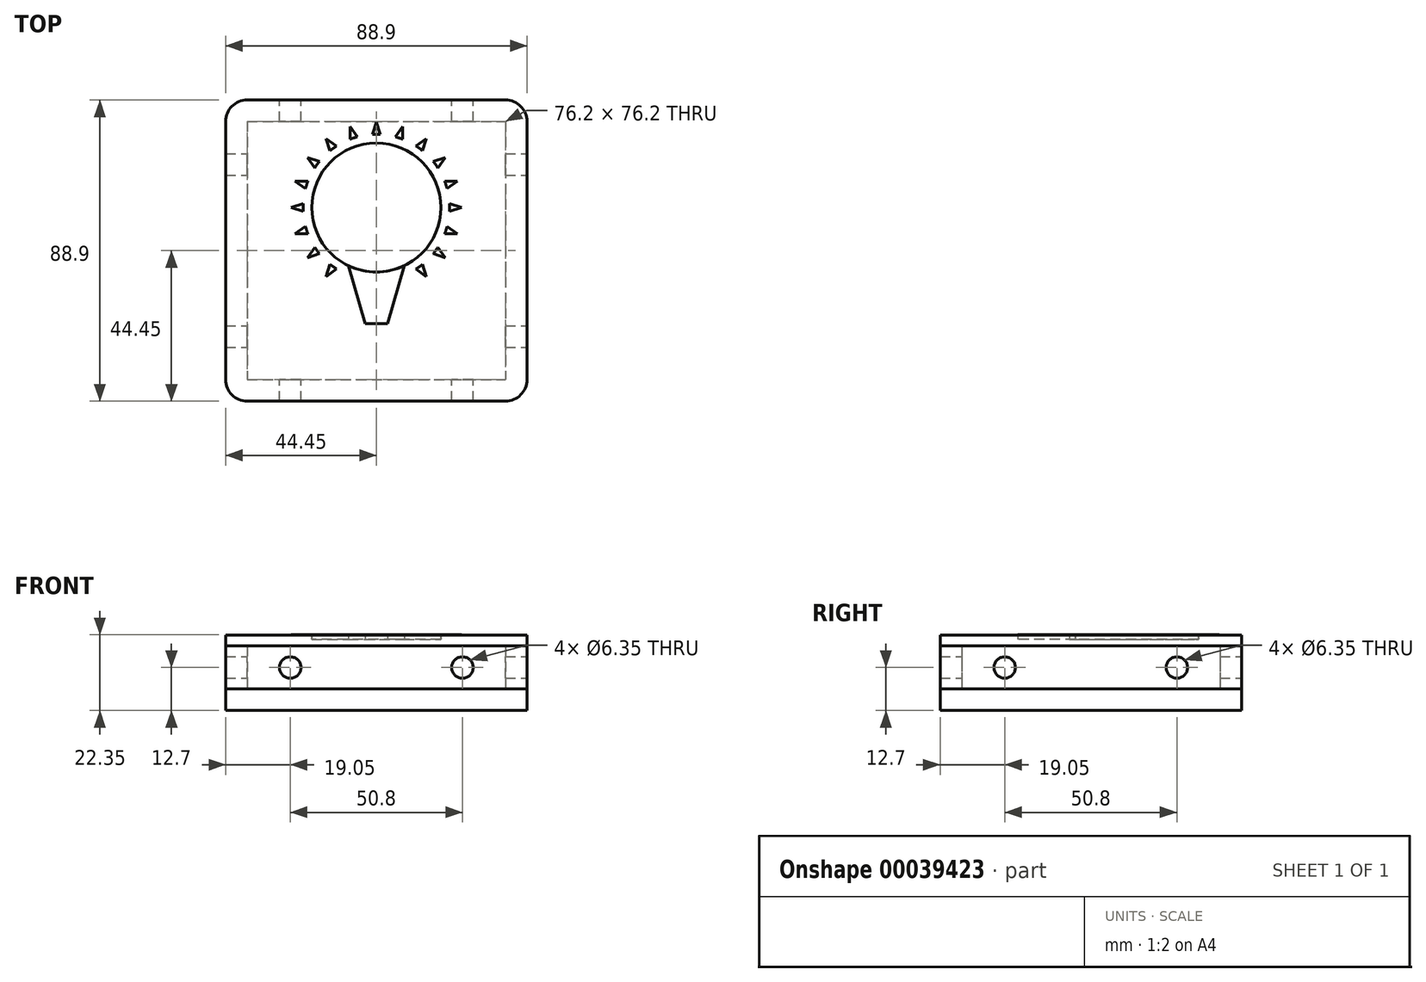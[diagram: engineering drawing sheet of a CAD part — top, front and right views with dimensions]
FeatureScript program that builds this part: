
annotation { "Feature Type Name" : "Feature", "Feature Type Description" : "" }
export const myFeature = defineFeature(function(context is Context, id is Id, definition is map)
    precondition{}
    {
        {
            var Q0;
            Q0=qCreatedBy(makeId("Top.planeOp"),FACE);
            var sketch = newSketch(context, id + "F0", { "sketchPlane" : qUnion([Q0])});
            skLineSegment(sketch, "E0.rect.bottom", {"start": v(-38.1, 44.45) * mm, "end": v(38.1, 44.45) * mm});
            skLineSegment(sketch, "E0.rect.top", {"start": v(-38.1, -44.45) * mm, "end": v(38.1, -44.45) * mm});
            skLineSegment(sketch, "E0.rect.left", {"start": v(-44.45, 38.1) * mm, "end": v(-44.45, -38.1) * mm});
            skLineSegment(sketch, "E0.rect.right", {"start": v(44.45, 38.1) * mm, "end": v(44.45, -38.1) * mm});
            skPoint(sketch, "E0.rect.middle", {"position": v(0, 0) * mm});
            skPoint(sketch, "E1.visualSharp", {"position": v(-44.45, 44.45) * mm});
            skArc(sketch, "E1.filletArc", {"start": v(-38.1, 44.45) * mm, "mid": v(-42.6, 42.6) * mm, "end": v(-44.45, 38.1) * mm});
            skPoint(sketch, "E2.visualSharp", {"position": v(44.45, 44.45) * mm});
            skArc(sketch, "E2.filletArc", {"start": v(44.45, 38.1) * mm, "mid": v(42.6, 42.6) * mm, "end": v(38.1, 44.45) * mm});
            skPoint(sketch, "E3.visualSharp", {"position": v(44.45, -44.45) * mm});
            skArc(sketch, "E3.filletArc", {"start": v(38.1, -44.45) * mm, "mid": v(42.6, -42.6) * mm, "end": v(44.45, -38.1) * mm});
            skPoint(sketch, "E4.visualSharp", {"position": v(-44.45, -44.45) * mm});
            skArc(sketch, "E4.filletArc", {"start": v(-44.45, -38.1) * mm, "mid": v(-42.6, -42.6) * mm, "end": v(-38.1, -44.45) * mm});
            skSolve(sketch);
        }
        {
            var Q0;
            Q0 = qSketchRegion(id + "F0", true);
            extrude(context, id + "F1", {"entities" : qUnion([Q0]), "depth" : 6.35 * mm});
        }
        {
            var Q0;
            Q0=makeQuery(id+"F1.opExtrude","CAP_FACE",FACE,{"disambiguationData":[OSD([sQuery(id+"F0.wireOp",EDGE,"E0.rect.bottom"),sQuery(id+"F0.wireOp",EDGE,"E0.rect.top"),sQuery(id+"F0.wireOp",EDGE,"E0.rect.left"),sQuery(id+"F0.wireOp",EDGE,"E0.rect.right"),sQuery(id+"F0.wireOp",EDGE,"E1.filletArc"),sQuery(id+"F0.wireOp",EDGE,"E2.filletArc"),sQuery(id+"F0.wireOp",EDGE,"E3.filletArc"),sQuery(id+"F0.wireOp",EDGE,"E4.filletArc")])],"isStart":false});
            var sketch = newSketch(context, id + "F2", { "sketchPlane" : qUnion([Q0])});
            skArc(sketch, "E5.0", {"start": v(-38.1, 44.45) * mm, "mid": v(-42.6, 42.6) * mm, "end": v(-44.45, 38.1) * mm});
            skLineSegment(sketch, "E6.0", {"start": v(-38.1, 44.45) * mm, "end": v(38.1, 44.45) * mm});
            skArc(sketch, "E7.0", {"start": v(44.45, 38.1) * mm, "mid": v(42.6, 42.6) * mm, "end": v(38.1, 44.45) * mm});
            skLineSegment(sketch, "E8.0", {"start": v(44.45, 38.1) * mm, "end": v(44.45, -38.1) * mm});
            skArc(sketch, "E9.0", {"start": v(38.1, -44.45) * mm, "mid": v(42.6, -42.6) * mm, "end": v(44.45, -38.1) * mm});
            skLineSegment(sketch, "E10.0", {"start": v(-38.1, -44.45) * mm, "end": v(38.1, -44.45) * mm});
            skArc(sketch, "E11.0", {"start": v(-44.45, -38.1) * mm, "mid": v(-42.6, -42.6) * mm, "end": v(-38.1, -44.45) * mm});
            skLineSegment(sketch, "E12.0", {"start": v(-44.45, 38.1) * mm, "end": v(-44.45, -38.1) * mm});
            skLineSegment(sketch, "E13", {"start": v(-44.45, -38.1) * mm, "end": v(44.45, -38.1) * mm});
            skLineSegment(sketch, "E14", {"start": v(-44.45, 38.1) * mm, "end": v(44.45, 38.1) * mm});
            skLineSegment(sketch, "E15", {"start": v(38.1, 38.1) * mm, "end": v(38.1, -38.1) * mm});
            skLineSegment(sketch, "E16", {"start": v(-38.1, 38.1) * mm, "end": v(-38.1, -38.1) * mm});
            skSolve(sketch);
        }
        {
            var Q0;
            Q0 = qSketchRegion(id + "F2", true);
            extrude(context, id + "F3", {"entities" : qUnion([Q0]), "depth" : 12.7 * mm});
        }
        {
            var Q0;
            Q0=makeQuery(id+"F3.opExtrude","CAP_FACE",FACE,{"disambiguationData":[OSD([sQuery(id+"F2.wireOp",EDGE,"E5.0"),sQuery(id+"F2.wireOp",EDGE,"E6.0"),sQuery(id+"F2.wireOp",EDGE,"E7.0"),sQuery(id+"F2.wireOp",EDGE,"E8.0"),sQuery(id+"F2.wireOp",EDGE,"E9.0"),sQuery(id+"F2.wireOp",EDGE,"E10.0"),sQuery(id+"F2.wireOp",EDGE,"E11.0"),sQuery(id+"F2.wireOp",EDGE,"E12.0"),sQuery(id+"F2.wireOp",EDGE,"E13"),sQuery(id+"F2.wireOp",EDGE,"E14"),sQuery(id+"F2.wireOp",EDGE,"E15"),sQuery(id+"F2.wireOp",EDGE,"E16")])],"isStart":false});
            var sketch = newSketch(context, id + "F4", { "sketchPlane" : qUnion([Q0])});
            skArc(sketch, "E17.0", {"start": v(-38.1, 44.45) * mm, "mid": v(-42.6, 42.6) * mm, "end": v(-44.45, 38.1) * mm});
            skLineSegment(sketch, "E18.0", {"start": v(-38.1, 44.45) * mm, "end": v(38.1, 44.45) * mm});
            skArc(sketch, "E19.0", {"start": v(44.45, 38.1) * mm, "mid": v(42.6, 42.6) * mm, "end": v(38.1, 44.45) * mm});
            skLineSegment(sketch, "E20.0", {"start": v(44.45, 38.1) * mm, "end": v(44.45, -38.1) * mm});
            skArc(sketch, "E21.0", {"start": v(38.1, -44.45) * mm, "mid": v(42.6, -42.6) * mm, "end": v(44.45, -38.1) * mm});
            skLineSegment(sketch, "E22.0", {"start": v(-38.1, -44.45) * mm, "end": v(38.1, -44.45) * mm});
            skArc(sketch, "E23.0", {"start": v(-44.45, -38.1) * mm, "mid": v(-42.6, -42.6) * mm, "end": v(-38.1, -44.45) * mm});
            skLineSegment(sketch, "E24.0", {"start": v(-44.45, 38.1) * mm, "end": v(-44.45, -38.1) * mm});
            skSolve(sketch);
        }
        {
            var Q0;
            Q0 = qSketchRegion(id + "F4", true);
            extrude(context, id + "F5", {"entities" : qUnion([Q0]), "depth" : 3.17 * mm});
        }
        {
            var Q0;
            Q0=makeQuery(id+"F3.opExtrude","SWEPT_FACE",FACE,{"disambiguationData":[OSD([sQuery(id+"F2.wireOp",EDGE,"E8.0")])]});
            var sketch = newSketch(context, id + "F6", { "sketchPlane" : qUnion([Q0])});
            skCircle(sketch, "E25", {"center": v(25.4, 12.7) * mm, "radius": 3.18 * mm});
            skPoint(sketch, "E25.centerSnap0", {"position": v(38.1, 12.7) * mm});
            skCircle(sketch, "E26", {"center": v(-25.4, 12.7) * mm, "radius": 3.18 * mm});
            skPoint(sketch, "E26.centerSnap0", {"position": v(-38.1, 12.7) * mm});
            skSolve(sketch);
        }
        {
            var Q0;
            Q0 = qSketchRegion(id + "F6", true);
            extrude(context, id + "F7", {"entities" : qUnion([Q0]), "operationType" : NewBodyOperationType.REMOVE, "endBound" : BoundingType.THROUGH_ALL, "oppositeDirection" : true, "depth" : 25.4 * mm});
        }
        {
            var Q0;
            Q0=makeQuery(id+"F3.opExtrude","SWEPT_FACE",FACE,{"disambiguationData":[OSD([sQuery(id+"F2.wireOp",EDGE,"E6.0")])]});
            var sketch = newSketch(context, id + "F8", { "sketchPlane" : qUnion([Q0])});
            skCircle(sketch, "E27", {"center": v(25.4, 12.7) * mm, "radius": 3.18 * mm});
            skPoint(sketch, "E27.centerSnap0", {"position": v(38.1, 12.7) * mm});
            skCircle(sketch, "E28", {"center": v(-25.4, 12.7) * mm, "radius": 3.18 * mm});
            skSolve(sketch);
        }
        {
            var Q0;
            Q0 = qSketchRegion(id + "F8", true);
            extrude(context, id + "F9", {"entities" : qUnion([Q0]), "operationType" : NewBodyOperationType.REMOVE, "endBound" : BoundingType.THROUGH_ALL, "oppositeDirection" : true, "depth" : 25.4 * mm});
        }
        {
            var Q0;
            Q0=makeQuery(id+"F5.opExtrude","CAP_FACE",FACE,{"disambiguationData":[OSD([sQuery(id+"F4.wireOp",EDGE,"E17.0"),sQuery(id+"F4.wireOp",EDGE,"E18.0"),sQuery(id+"F4.wireOp",EDGE,"E19.0"),sQuery(id+"F4.wireOp",EDGE,"E20.0"),sQuery(id+"F4.wireOp",EDGE,"E21.0"),sQuery(id+"F4.wireOp",EDGE,"E22.0"),sQuery(id+"F4.wireOp",EDGE,"E23.0"),sQuery(id+"F4.wireOp",EDGE,"E24.0")])],"isStart":false});
            var sketch = newSketch(context, id + "F10", { "sketchPlane" : qUnion([Q0])});
            skLineSegment(sketch, "E29.rect.bottom", {"start": v(-10.16, 22.86) * mm, "end": v(-3.8, 22.86) * mm});
            skLineSegment(sketch, "E29.rect.top", {"start": v(-10.16, -22.86) * mm, "end": v(10.16, -22.86) * mm});
            skLineSegment(sketch, "E29.rect.left", {"start": v(-12.7, 20.32) * mm, "end": v(-12.7, -20.32) * mm});
            skLineSegment(sketch, "E29.rect.right", {"start": v(12.7, 20.32) * mm, "end": v(12.7, -20.32) * mm});
            skPoint(sketch, "E29.rect.middle", {"position": v(0, 0) * mm});
            skLineSegment(sketch, "E30.rect.top", {"start": v(3.81, 29.21) * mm, "end": v(-3.8, 29.21) * mm});
            skLineSegment(sketch, "E30.rect.left", {"start": v(3.81, 22.86) * mm, "end": v(3.81, 29.21) * mm});
            skLineSegment(sketch, "E30.rect.right", {"start": v(-3.8, 22.86) * mm, "end": v(-3.8, 29.21) * mm});
            skPoint(sketch, "E30.rect.middle", {"position": v(0, 26.04) * mm});
            skLineSegment(sketch, "E31.trimOffspring", {"start": v(3.81, 22.86) * mm, "end": v(10.16, 22.86) * mm});
            skPoint(sketch, "E32.visualSharp", {"position": v(-12.7, 22.86) * mm});
            skArc(sketch, "E32.filletArc", {"start": v(-10.16, 22.86) * mm, "mid": v(-11.96, 22.12) * mm, "end": v(-12.7, 20.32) * mm});
            skPoint(sketch, "E33.visualSharp", {"position": v(12.7, 22.86) * mm});
            skArc(sketch, "E33.filletArc", {"start": v(12.7, 20.32) * mm, "mid": v(11.96, 22.12) * mm, "end": v(10.16, 22.86) * mm});
            skPoint(sketch, "E34.visualSharp", {"position": v(12.7, -22.86) * mm});
            skArc(sketch, "E34.filletArc", {"start": v(10.16, -22.86) * mm, "mid": v(11.96, -22.12) * mm, "end": v(12.7, -20.32) * mm});
            skPoint(sketch, "E35.visualSharp", {"position": v(-12.7, -22.86) * mm});
            skArc(sketch, "E35.filletArc", {"start": v(-12.7, -20.32) * mm, "mid": v(-11.96, -22.12) * mm, "end": v(-10.16, -22.86) * mm});
            skLineSegment(sketch, "E36", {"start": v(-2.4, 27.75) * mm, "end": v(2.54, 27.75) * mm});
            skLineSegment(sketch, "E37", {"start": v(2.54, 27.75) * mm, "end": v(2.54, 21.52) * mm});
            skLineSegment(sketch, "E38", {"start": v(2.54, 21.52) * mm, "end": v(10.71, 21.52) * mm});
            skLineSegment(sketch, "E39", {"start": v(10.71, 21.52) * mm, "end": v(10.71, -20.32) * mm});
            skLineSegment(sketch, "E40", {"start": v(10.71, -20.32) * mm, "end": v(-11.48, -20.32) * mm});
            skLineSegment(sketch, "E41", {"start": v(-11.48, -20.32) * mm, "end": v(-11.48, 21.52) * mm});
            skLineSegment(sketch, "E42", {"start": v(-11.48, 21.52) * mm, "end": v(-2.4, 21.52) * mm});
            skLineSegment(sketch, "E43", {"start": v(-2.4, 21.52) * mm, "end": v(-2.4, 27.75) * mm});
            skLineSegment(sketch, "E44.rect.bottom", {"start": v(-9.14, 19.32) * mm, "end": v(9.14, 19.32) * mm});
            skLineSegment(sketch, "E44.rect.top", {"start": v(-9.14, 6.86) * mm, "end": v(9.14, 6.86) * mm});
            skLineSegment(sketch, "E44.rect.left", {"start": v(-9.14, 19.32) * mm, "end": v(-9.14, 6.86) * mm});
            skLineSegment(sketch, "E44.rect.right", {"start": v(9.14, 19.32) * mm, "end": v(9.14, 6.86) * mm});
            skPoint(sketch, "E44.rect.middle", {"position": v(0, 13.09) * mm});
            skLineSegment(sketch, "E45.bottom", {"start": v(-9.14, 4.65) * mm, "end": v(9.14, 4.65) * mm});
            skLineSegment(sketch, "E45.top", {"start": v(-9.14, -6.5) * mm, "end": v(9.14, -6.5) * mm});
            skLineSegment(sketch, "E45.left", {"start": v(-9.14, 4.65) * mm, "end": v(-9.14, -6.5) * mm});
            skLineSegment(sketch, "E45.right", {"start": v(9.14, 4.65) * mm, "end": v(9.14, -6.5) * mm});
            skLineSegment(sketch, "E46.bottom", {"start": v(-9.14, -8.32) * mm, "end": v(9.14, -8.32) * mm});
            skLineSegment(sketch, "E46.top", {"start": v(-9.14, -18.83) * mm, "end": v(9.14, -18.83) * mm});
            skLineSegment(sketch, "E46.left", {"start": v(-9.14, -8.32) * mm, "end": v(-9.14, -18.83) * mm});
            skLineSegment(sketch, "E46.right", {"start": v(9.14, -8.32) * mm, "end": v(9.14, -18.83) * mm});
            skSolve(sketch);
        }
        {
            var Q0;
            Q0 = qSketchRegion(id + "F10", true);
            var Q1;
            Q1=makeQuery(id+"F10.imprint","IMPRINT",FACE,{"disambiguationData":[TD([[makeQuery(id+"F10.imprint","IMPRINT",EDGE,{"derivedFrom":sQuery(id+"F10.wireOp",EDGE,"E44.rect.bottom")}),-1.0]])]});
            var Q2;
            Q2=makeQuery(id+"F10.imprint","IMPRINT",FACE,{"disambiguationData":[TD([[makeQuery(id+"F10.imprint","IMPRINT",EDGE,{"derivedFrom":sQuery(id+"F10.wireOp",EDGE,"E45.bottom")}),-1.0]])]});
            var Q3;
            Q3=makeQuery(id+"F10.imprint","IMPRINT",FACE,{"disambiguationData":[TD([[makeQuery(id+"F10.imprint","IMPRINT",EDGE,{"derivedFrom":sQuery(id+"F10.wireOp",EDGE,"E46.bottom")}),-1.0]])]});
            extrude(context, id + "F11", {"entities" : qUnion([Q0, Q1, Q2, Q3]), "operationType" : NewBodyOperationType.REMOVE, "oppositeDirection" : true, "depth" : 1.27 * mm});
        }
        {
            var Q0;
            Q0=makeQuery(id+"F3.opExtrude","CAP_FACE",FACE,{"disambiguationData":[OSD([sQuery(id+"F2.wireOp",EDGE,"E5.0"),sQuery(id+"F2.wireOp",EDGE,"E6.0"),sQuery(id+"F2.wireOp",EDGE,"E7.0"),sQuery(id+"F2.wireOp",EDGE,"E8.0"),sQuery(id+"F2.wireOp",EDGE,"E9.0"),sQuery(id+"F2.wireOp",EDGE,"E10.0"),sQuery(id+"F2.wireOp",EDGE,"E11.0"),sQuery(id+"F2.wireOp",EDGE,"E12.0"),sQuery(id+"F2.wireOp",EDGE,"E13"),sQuery(id+"F2.wireOp",EDGE,"E14"),sQuery(id+"F2.wireOp",EDGE,"E15"),sQuery(id+"F2.wireOp",EDGE,"E16")])],"isStart":false});
            var sketch = newSketch(context, id + "F12", { "sketchPlane" : qUnion([Q0])});
            skArc(sketch, "E47.0", {"start": v(-38.1, 44.45) * mm, "mid": v(-42.6, 42.6) * mm, "end": v(-44.45, 38.1) * mm});
            skLineSegment(sketch, "E48.0", {"start": v(-38.1, 44.45) * mm, "end": v(38.1, 44.45) * mm});
            skArc(sketch, "E49.0", {"start": v(44.45, 38.1) * mm, "mid": v(42.6, 42.6) * mm, "end": v(38.1, 44.45) * mm});
            skLineSegment(sketch, "E50.0", {"start": v(44.45, 38.1) * mm, "end": v(44.45, -38.1) * mm});
            skArc(sketch, "E51.0", {"start": v(38.1, -44.45) * mm, "mid": v(42.6, -42.6) * mm, "end": v(44.45, -38.1) * mm});
            skLineSegment(sketch, "E52.0", {"start": v(-38.1, -44.45) * mm, "end": v(38.1, -44.45) * mm});
            skArc(sketch, "E53.0", {"start": v(-44.45, -38.1) * mm, "mid": v(-42.6, -42.6) * mm, "end": v(-38.1, -44.45) * mm});
            skLineSegment(sketch, "E54.0", {"start": v(-44.45, 38.1) * mm, "end": v(-44.45, -38.1) * mm});
            skSolve(sketch);
        }
        {
            var Q0;
            Q0 = qSketchRegion(id + "F12", true);
            extrude(context, id + "F13", {"entities" : qUnion([Q0]), "depth" : 3.17 * mm});
        }
        {
            var Q0;
            Q0=makeQuery(id+"F13.opExtrude","CAP_FACE",FACE,{"disambiguationData":[OSD([sQuery(id+"F12.wireOp",EDGE,"E47.0"),sQuery(id+"F12.wireOp",EDGE,"E48.0"),sQuery(id+"F12.wireOp",EDGE,"E49.0"),sQuery(id+"F12.wireOp",EDGE,"E50.0"),sQuery(id+"F12.wireOp",EDGE,"E51.0"),sQuery(id+"F12.wireOp",EDGE,"E52.0"),sQuery(id+"F12.wireOp",EDGE,"E53.0"),sQuery(id+"F12.wireOp",EDGE,"E54.0")])],"isStart":false});
            var sketch = newSketch(context, id + "F14", { "sketchPlane" : qUnion([Q0])});
            skCircle(sketch, "E55", {"center": v(0, 12.7) * mm, "radius": 19.05 * mm});
            skPoint(sketch, "E55.centerSnap0", {"position": v(0, -44.45) * mm});
            skLineSegment(sketch, "E56", {"start": v(-8.25, -4.47) * mm, "end": v(-3.35, -21.59) * mm});
            skLineSegment(sketch, "E57", {"start": v(-3.35, -21.59) * mm, "end": v(0, -21.59) * mm});
            skLineSegment(sketch, "E58", {"start": v(0, -21.59) * mm, "end": v(0, -6.35) * mm});
            skLineSegment(sketch, "E59.MirrorCS", {"start": v(3.35, -21.59) * mm, "end": v(0, -21.59) * mm});
            skLineSegment(sketch, "E60.MirrorCS", {"start": v(8.26, -4.47) * mm, "end": v(3.35, -21.6) * mm});
            skSolve(sketch);
        }
        {
            var Q0;
            Q0 = qSketchRegion(id + "F14", true);
            extrude(context, id + "F15", {"entities" : qUnion([Q0]), "operationType" : NewBodyOperationType.REMOVE, "oppositeDirection" : true, "depth" : 1.27 * mm});
        }
        {
            var Q0;
            Q0=makeQuery(id+"F15.boolean.opBoolean","COPY",FACE,{"derivedFrom":makeQuery(id+"F15.opExtrude","CAP_FACE",FACE,{"disambiguationData":[OSD([sQuery(id+"F14.wireOp",EDGE,"E55"),sQuery(id+"F14.wireOp",EDGE,"E56"),sQuery(id+"F14.wireOp",EDGE,"E57"),sQuery(id+"F14.wireOp",EDGE,"E59.MirrorCS"),sQuery(id+"F14.wireOp",EDGE,"E60.MirrorCS")])],"isStart":false})});
            var sketch = newSketch(context, id + "F16", { "sketchPlane" : qUnion([Q0])});
            skArc(sketch, "E61.0", {"start": v(8.26, -4.47) * mm, "mid": v(0, 31.75) * mm, "end": v(-8.25, -4.47) * mm});
            skCircle(sketch, "E62", {"center": v(0, 12.7) * mm, "radius": 19.05 * mm});
            skSolve(sketch);
        }
        {
            var Q0;
            Q0 = qSketchRegion(id + "F16", true);
            extrude(context, id + "F17", {"entities" : qUnion([Q0]), "depth" : 1.4 * mm});
        }
        {
            var Q0;
            Q0=makeQuery(id+"F15.boolean.opBoolean","COPY",FACE,{"derivedFrom":makeQuery(id+"F15.opExtrude","CAP_FACE",FACE,{"disambiguationData":[OSD([sQuery(id+"F14.wireOp",EDGE,"E55"),sQuery(id+"F14.wireOp",EDGE,"E56"),sQuery(id+"F14.wireOp",EDGE,"E57"),sQuery(id+"F14.wireOp",EDGE,"E59.MirrorCS"),sQuery(id+"F14.wireOp",EDGE,"E60.MirrorCS")])],"isStart":false})});
            var sketch = newSketch(context, id + "F18", { "sketchPlane" : qUnion([Q0])});
            skArc(sketch, "E63.0.0", {"start": v(8.26, -4.47) * mm, "mid": v(0, 31.75) * mm, "end": v(-8.25, -4.47) * mm});
            skLineSegment(sketch, "E63.0.1", {"start": v(-8.25, -4.47) * mm, "end": v(-3.35, -21.59) * mm});
            skLineSegment(sketch, "E63.0.2", {"start": v(-3.35, -21.59) * mm, "end": v(3.35, -21.59) * mm});
            skLineSegment(sketch, "E63.0.3", {"start": v(3.35, -21.6) * mm, "end": v(8.26, -4.47) * mm});
            skCircle(sketch, "E64.0", {"center": v(0, 12.7) * mm, "radius": 19.05 * mm});
            skSolve(sketch);
        }
        {
            var Q0;
            {var subQ2=sQuery(id+"F18.wireOp",EDGE,"E63.0.1");Q0=makeQuery(id+"F18.imprint","IMPRINT",FACE,{"disambiguationData":[TD([[makeQuery(id+"F18.imprint","IMPRINT",EDGE,{"derivedFrom":subQ2}),1.0]])]});}
            extrude(context, id + "F19", {"entities" : qUnion([Q0]), "depth" : 1.4 * mm});
        }
        {
            var Q0;
            Q0=makeQuery(id+"F13.opExtrude","CAP_FACE",FACE,{"disambiguationData":[OSD([sQuery(id+"F12.wireOp",EDGE,"E47.0"),sQuery(id+"F12.wireOp",EDGE,"E48.0"),sQuery(id+"F12.wireOp",EDGE,"E49.0"),sQuery(id+"F12.wireOp",EDGE,"E50.0"),sQuery(id+"F12.wireOp",EDGE,"E51.0"),sQuery(id+"F12.wireOp",EDGE,"E52.0"),sQuery(id+"F12.wireOp",EDGE,"E53.0"),sQuery(id+"F12.wireOp",EDGE,"E54.0")])],"isStart":false});
            var sketch = newSketch(context, id + "F20", { "sketchPlane" : qUnion([Q0])});
            skCircle(sketch, "E65", {"center": v(0, 12.7) * mm, "radius": 21.61 * mm});
            skLineSegment(sketch, "E66", {"start": v(0, 34.31) * mm, "end": v(0, 37.87) * mm});
            skPoint(sketch, "E66.startSnap0", {"position": v(0, 31.75) * mm});
            skLineSegment(sketch, "E67", {"start": v(0, 37.87) * mm, "end": v(-1.17, 34.28) * mm});
            skLineSegment(sketch, "E68.MirrorCS", {"start": v(0, 37.87) * mm, "end": v(1.17, 34.28) * mm});
            skLineSegment(sketch, "E69.1.0", {"start": v(-7.78, 36.64) * mm, "end": v(-5.56, 33.59) * mm});
            skLineSegment(sketch, "E69.1.1", {"start": v(-7.78, 36.64) * mm, "end": v(-7.78, 32.86) * mm});
            skLineSegment(sketch, "E69.2.0", {"start": v(-14.8, 33.07) * mm, "end": v(-11.74, 30.85) * mm});
            skLineSegment(sketch, "E69.2.1", {"start": v(-14.8, 33.07) * mm, "end": v(-13.63, 29.47) * mm});
            skLineSegment(sketch, "E69.3.0", {"start": v(-20.37, 27.5) * mm, "end": v(-16.77, 26.33) * mm});
            skLineSegment(sketch, "E69.3.1", {"start": v(-20.37, 27.5) * mm, "end": v(-18.15, 24.44) * mm});
            skLineSegment(sketch, "E69.4.0", {"start": v(-23.94, 20.48) * mm, "end": v(-20.16, 20.48) * mm});
            skLineSegment(sketch, "E69.4.1", {"start": v(-23.94, 20.48) * mm, "end": v(-20.89, 18.26) * mm});
            skLineSegment(sketch, "E69.5.0", {"start": v(-25.17, 12.7) * mm, "end": v(-21.58, 13.87) * mm});
            skLineSegment(sketch, "E69.5.1", {"start": v(-25.17, 12.7) * mm, "end": v(-21.58, 11.53) * mm});
            skLineSegment(sketch, "E69.6.0", {"start": v(-23.94, 4.92) * mm, "end": v(-20.89, 7.14) * mm});
            skLineSegment(sketch, "E69.6.1", {"start": v(-23.94, 4.92) * mm, "end": v(-20.16, 4.92) * mm});
            skLineSegment(sketch, "E69.7.0", {"start": v(-20.37, -2.1) * mm, "end": v(-18.15, 0.96) * mm});
            skLineSegment(sketch, "E69.7.1", {"start": v(-20.37, -2.1) * mm, "end": v(-16.77, -0.93) * mm});
            skLineSegment(sketch, "E69.8.0", {"start": v(-14.8, -7.67) * mm, "end": v(-13.63, -4.07) * mm});
            skLineSegment(sketch, "E69.8.1", {"start": v(-14.8, -7.67) * mm, "end": v(-11.74, -5.45) * mm});
            skLineSegment(sketch, "E69.12.0", {"start": v(14.8, -7.67) * mm, "end": v(11.74, -5.45) * mm});
            skLineSegment(sketch, "E69.12.1", {"start": v(14.8, -7.67) * mm, "end": v(13.63, -4.07) * mm});
            skLineSegment(sketch, "E69.13.0", {"start": v(20.37, -2.1) * mm, "end": v(16.77, -0.93) * mm});
            skLineSegment(sketch, "E69.13.1", {"start": v(20.37, -2.1) * mm, "end": v(18.15, 0.96) * mm});
            skLineSegment(sketch, "E69.14.0", {"start": v(23.94, 4.92) * mm, "end": v(20.16, 4.92) * mm});
            skLineSegment(sketch, "E69.14.1", {"start": v(23.94, 4.92) * mm, "end": v(20.89, 7.14) * mm});
            skLineSegment(sketch, "E69.15.0", {"start": v(25.17, 12.7) * mm, "end": v(21.58, 11.53) * mm});
            skLineSegment(sketch, "E69.15.1", {"start": v(25.17, 12.7) * mm, "end": v(21.58, 13.87) * mm});
            skLineSegment(sketch, "E69.16.0", {"start": v(23.94, 20.48) * mm, "end": v(20.89, 18.26) * mm});
            skLineSegment(sketch, "E69.16.1", {"start": v(23.94, 20.48) * mm, "end": v(20.16, 20.48) * mm});
            skLineSegment(sketch, "E69.17.0", {"start": v(20.37, 27.5) * mm, "end": v(18.15, 24.44) * mm});
            skLineSegment(sketch, "E69.17.1", {"start": v(20.37, 27.5) * mm, "end": v(16.77, 26.33) * mm});
            skLineSegment(sketch, "E69.18.0", {"start": v(14.8, 33.07) * mm, "end": v(13.63, 29.47) * mm});
            skLineSegment(sketch, "E69.18.1", {"start": v(14.8, 33.07) * mm, "end": v(11.74, 30.85) * mm});
            skLineSegment(sketch, "E69.19.0", {"start": v(7.78, 36.64) * mm, "end": v(7.78, 32.86) * mm});
            skLineSegment(sketch, "E69.19.1", {"start": v(7.78, 36.64) * mm, "end": v(5.56, 33.59) * mm});
            skSolve(sketch);
        }
        {
            var Q0;
            {var subQ0=sQuery(id+"F20.wireOp",EDGE,"E66");Q0=makeQuery(id+"F20.imprint","IMPRINT",FACE,{"disambiguationData":[TD([[makeQuery(id+"F20.imprint","IMPRINT",EDGE,{"derivedFrom":subQ0}),1.0]])]});}
            var Q1;
            {var subQ1=sQuery(id+"F20.wireOp",EDGE,"E66");Q1=makeQuery(id+"F20.imprint","IMPRINT",FACE,{"disambiguationData":[TD([[makeQuery(id+"F20.imprint","IMPRINT",EDGE,{"derivedFrom":subQ1}),-1.0]])]});}
            var Q2;
            {var subQ1=sQuery(id+"F20.wireOp",EDGE,"E69.1.0");Q2=makeQuery(id+"F20.imprint","IMPRINT",FACE,{"disambiguationData":[TD([[makeQuery(id+"F20.imprint","IMPRINT",EDGE,{"derivedFrom":subQ1}),-1.0]])]});}
            var Q3;
            {var subQ1=sQuery(id+"F20.wireOp",EDGE,"E69.2.0");Q3=makeQuery(id+"F20.imprint","IMPRINT",FACE,{"disambiguationData":[TD([[makeQuery(id+"F20.imprint","IMPRINT",EDGE,{"derivedFrom":subQ1}),-1.0]])]});}
            var Q4;
            {var subQ1=sQuery(id+"F20.wireOp",EDGE,"E69.19.0");Q4=makeQuery(id+"F20.imprint","IMPRINT",FACE,{"disambiguationData":[TD([[makeQuery(id+"F20.imprint","IMPRINT",EDGE,{"derivedFrom":subQ1}),-1.0]])]});}
            var Q5;
            {var subQ1=sQuery(id+"F20.wireOp",EDGE,"E69.18.0");Q5=makeQuery(id+"F20.imprint","IMPRINT",FACE,{"disambiguationData":[TD([[makeQuery(id+"F20.imprint","IMPRINT",EDGE,{"derivedFrom":subQ1}),-1.0]])]});}
            var Q6;
            {var subQ0=sQuery(id+"F20.wireOp",EDGE,"E69.17.0");Q6=makeQuery(id+"F20.imprint","IMPRINT",FACE,{"disambiguationData":[TD([[makeQuery(id+"F20.imprint","IMPRINT",EDGE,{"derivedFrom":subQ0}),-1.0]])]});}
            var Q7;
            {var subQ0=sQuery(id+"F20.wireOp",EDGE,"E69.16.0");Q7=makeQuery(id+"F20.imprint","IMPRINT",FACE,{"disambiguationData":[TD([[makeQuery(id+"F20.imprint","IMPRINT",EDGE,{"derivedFrom":subQ0}),-1.0]])]});}
            var Q8;
            {var subQ1=sQuery(id+"F20.wireOp",EDGE,"E69.15.0");Q8=makeQuery(id+"F20.imprint","IMPRINT",FACE,{"disambiguationData":[TD([[makeQuery(id+"F20.imprint","IMPRINT",EDGE,{"derivedFrom":subQ1}),-1.0]])]});}
            var Q9;
            {var subQ0=sQuery(id+"F20.wireOp",EDGE,"E69.14.0");Q9=makeQuery(id+"F20.imprint","IMPRINT",FACE,{"disambiguationData":[TD([[makeQuery(id+"F20.imprint","IMPRINT",EDGE,{"derivedFrom":subQ0}),-1.0]])]});}
            var Q10;
            {var subQ1=sQuery(id+"F20.wireOp",EDGE,"E69.13.0");Q10=makeQuery(id+"F20.imprint","IMPRINT",FACE,{"disambiguationData":[TD([[makeQuery(id+"F20.imprint","IMPRINT",EDGE,{"derivedFrom":subQ1}),-1.0]])]});}
            var Q11;
            {var subQ1=sQuery(id+"F20.wireOp",EDGE,"E69.12.0");Q11=makeQuery(id+"F20.imprint","IMPRINT",FACE,{"disambiguationData":[TD([[makeQuery(id+"F20.imprint","IMPRINT",EDGE,{"derivedFrom":subQ1}),-1.0]])]});}
            var Q12;
            {var subQ1=sQuery(id+"F20.wireOp",EDGE,"E69.8.0");Q12=makeQuery(id+"F20.imprint","IMPRINT",FACE,{"disambiguationData":[TD([[makeQuery(id+"F20.imprint","IMPRINT",EDGE,{"derivedFrom":subQ1}),-1.0]])]});}
            var Q13;
            {var subQ1=sQuery(id+"F20.wireOp",EDGE,"E69.7.0");Q13=makeQuery(id+"F20.imprint","IMPRINT",FACE,{"disambiguationData":[TD([[makeQuery(id+"F20.imprint","IMPRINT",EDGE,{"derivedFrom":subQ1}),-1.0]])]});}
            var Q14;
            {var subQ1=sQuery(id+"F20.wireOp",EDGE,"E69.6.0");Q14=makeQuery(id+"F20.imprint","IMPRINT",FACE,{"disambiguationData":[TD([[makeQuery(id+"F20.imprint","IMPRINT",EDGE,{"derivedFrom":subQ1}),-1.0]])]});}
            var Q15;
            {var subQ1=sQuery(id+"F20.wireOp",EDGE,"E69.5.0");Q15=makeQuery(id+"F20.imprint","IMPRINT",FACE,{"disambiguationData":[TD([[makeQuery(id+"F20.imprint","IMPRINT",EDGE,{"derivedFrom":subQ1}),-1.0]])]});}
            var Q16;
            {var subQ1=sQuery(id+"F20.wireOp",EDGE,"E69.4.0");Q16=makeQuery(id+"F20.imprint","IMPRINT",FACE,{"disambiguationData":[TD([[makeQuery(id+"F20.imprint","IMPRINT",EDGE,{"derivedFrom":subQ1}),-1.0]])]});}
            var Q17;
            {var subQ0=sQuery(id+"F20.wireOp",EDGE,"E69.3.0");Q17=makeQuery(id+"F20.imprint","IMPRINT",FACE,{"disambiguationData":[TD([[makeQuery(id+"F20.imprint","IMPRINT",EDGE,{"derivedFrom":subQ0}),-1.0]])]});}
            extrude(context, id + "F21", {"entities" : qUnion([Q0, Q1, Q2, Q3, Q4, Q5, Q6, Q7, Q8, Q9, Q10, Q11, Q12, Q13, Q14, Q15, Q16, Q17]), "operationType" : NewBodyOperationType.ADD, "depth" : 0.13 * mm});
        }
    });
